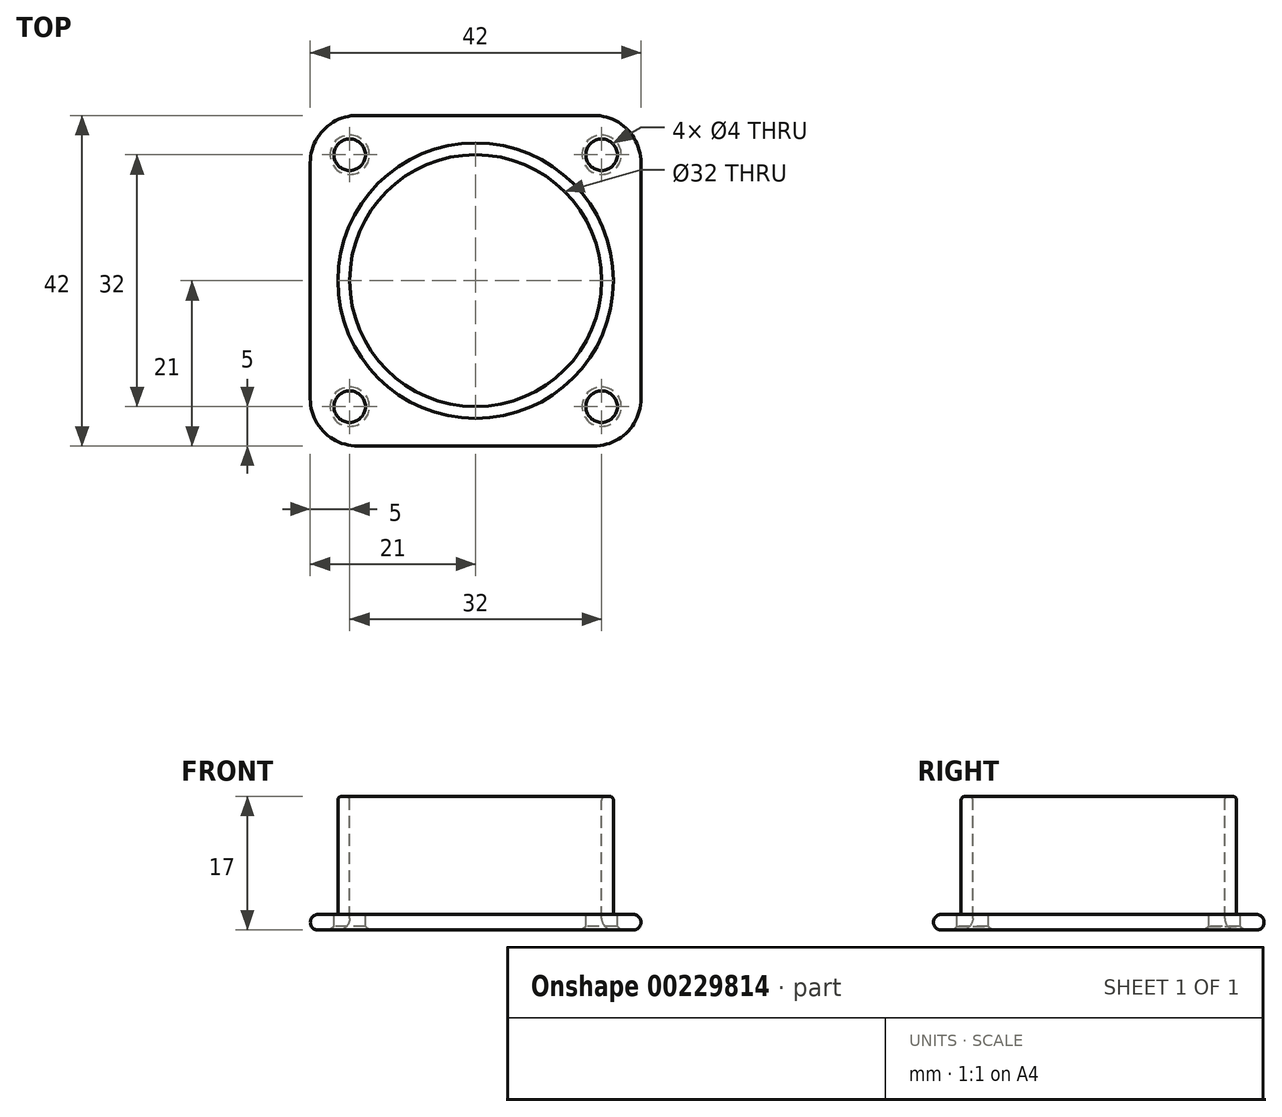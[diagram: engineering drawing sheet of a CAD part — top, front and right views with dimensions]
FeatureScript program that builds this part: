
annotation { "Feature Type Name" : "Feature", "Feature Type Description" : "" }
export const myFeature = defineFeature(function(context is Context, id is Id, definition is map)
    precondition{}
    {
        {
            var Q0;
            Q0=qCreatedBy(makeId("Top.planeOp"),FACE);
            var sketch = newSketch(context, id + "F0", { "sketchPlane" : qUnion([Q0])});
            skCircle(sketch, "E0", {"center": v(0, 0) * mm, "radius": 17.5 * mm});
            skLineSegment(sketch, "E1.bottom", {"start": v(21, 21) * mm, "end": v(-21, 21) * mm});
            skLineSegment(sketch, "E1.top", {"start": v(21, -21) * mm, "end": v(-21, -21) * mm});
            skLineSegment(sketch, "E1.left", {"start": v(21, 21) * mm, "end": v(21, -21) * mm});
            skLineSegment(sketch, "E1.right", {"start": v(-21, 21) * mm, "end": v(-21, -21) * mm});
            skLineSegment(sketch, "E2.bottom", {"start": v(-16, 16) * mm, "end": v(16, 16) * mm, "construction": true});
            skLineSegment(sketch, "E2.top", {"start": v(-16, -16) * mm, "end": v(16, -16) * mm, "construction": true});
            skLineSegment(sketch, "E2.left", {"start": v(-16, 16) * mm, "end": v(-16, -16) * mm, "construction": true});
            skLineSegment(sketch, "E2.right", {"start": v(16, 16) * mm, "end": v(16, -16) * mm, "construction": true});
            skCircle(sketch, "E3", {"center": v(0, 0) * mm, "radius": 16 * mm});
            skCircle(sketch, "E4", {"center": v(-16, 16) * mm, "radius": 2 * mm});
            skCircle(sketch, "E5", {"center": v(16, 16) * mm, "radius": 2 * mm});
            skCircle(sketch, "E6", {"center": v(16, -16) * mm, "radius": 2 * mm});
            skCircle(sketch, "E7", {"center": v(-16, -16) * mm, "radius": 2 * mm});
            skSolve(sketch);
        }
        {
            var Q0;
            Q0=makeQuery(id+"F0.imprint","IMPRINT",FACE,{"disambiguationData":[TD([[makeQuery(id+"F0.imprint","IMPRINT",EDGE,{"derivedFrom":sQuery(id+"F0.wireOp",EDGE,"E0")}),-1.0]])]});
            var Q1;
            Q1=makeQuery(id+"F0.imprint","IMPRINT",FACE,{"disambiguationData":[TD([[makeQuery(id+"F0.imprint","IMPRINT",EDGE,{"derivedFrom":sQuery(id+"F0.wireOp",EDGE,"E0")}),1.0]])]});
            extrude(context, id + "F1", {"entities" : qUnion([Q0, Q1]), "oppositeDirection" : true, "depth" : 2 * mm});
        }
        {
            var Q0;
            Q0=makeQuery(id+"F0.imprint","IMPRINT",FACE,{"disambiguationData":[TD([[makeQuery(id+"F0.imprint","IMPRINT",EDGE,{"derivedFrom":sQuery(id+"F0.wireOp",EDGE,"E0")}),1.0]])]});
            extrude(context, id + "F2", {"entities" : qUnion([Q0]), "operationType" : NewBodyOperationType.ADD, "depth" : 15 * mm});
        }
        {
            var Q0;
            Q0=makeQuery(id+"F1.opExtrude","SWEPT_EDGE",EDGE,{"disambiguationData":[OSD([sQuery(id+"F0.wireOp",EDGE,"E1.bottom"),sQuery(id+"F0.wireOp",EDGE,"E1.right")])]});
            var Q1;
            Q1=makeQuery(id+"F1.opExtrude","SWEPT_EDGE",EDGE,{"disambiguationData":[OSD([sQuery(id+"F0.wireOp",EDGE,"E1.top"),sQuery(id+"F0.wireOp",EDGE,"E1.right")])]});
            var Q2;
            Q2=makeQuery(id+"F1.opExtrude","SWEPT_EDGE",EDGE,{"disambiguationData":[OSD([sQuery(id+"F0.wireOp",EDGE,"E1.top"),sQuery(id+"F0.wireOp",EDGE,"E1.left")])]});
            var Q3;
            Q3=makeQuery(id+"F1.opExtrude","SWEPT_EDGE",EDGE,{"disambiguationData":[OSD([sQuery(id+"F0.wireOp",EDGE,"E1.bottom"),sQuery(id+"F0.wireOp",EDGE,"E1.left")])]});
            fillet(context, id + "F3", {"entities" : qUnion([Q0, Q1, Q2, Q3]), "radius" : 6 * mm, "tangentPropagation" : true, "allowEdgeOverflow" : false});
        }
        {
            var Q0;
            Q0=makeQuery(id+"F1.opExtrude","SWEPT_FACE",FACE,{"disambiguationData":[OSD([sQuery(id+"F0.wireOp",EDGE,"E1.left")])]});
            var Q1;
            Q1=makeQuery(id+"F3.opFillet","BLEND_FACE",FACE,{"disambiguationData":[OSD([sQuery(id+"F0.wireOp",EDGE,"E1.top"),sQuery(id+"F0.wireOp",EDGE,"E1.left")])]});
            var Q2;
            Q2=makeQuery(id+"F3.opFillet","BLEND_FACE",FACE,{"disambiguationData":[OSD([sQuery(id+"F0.wireOp",EDGE,"E1.bottom"),sQuery(id+"F0.wireOp",EDGE,"E1.left")])]});
            var Q3;
            Q3=makeQuery(id+"F1.opExtrude","SWEPT_FACE",FACE,{"disambiguationData":[OSD([sQuery(id+"F0.wireOp",EDGE,"E1.bottom")])]});
            var Q4;
            Q4=makeQuery(id+"F3.opFillet","BLEND_FACE",FACE,{"disambiguationData":[OSD([sQuery(id+"F0.wireOp",EDGE,"E1.bottom"),sQuery(id+"F0.wireOp",EDGE,"E1.right")])]});
            var Q5;
            Q5=makeQuery(id+"F1.opExtrude","SWEPT_FACE",FACE,{"disambiguationData":[OSD([sQuery(id+"F0.wireOp",EDGE,"E1.right")])]});
            var Q6;
            Q6=makeQuery(id+"F3.opFillet","BLEND_FACE",FACE,{"disambiguationData":[OSD([sQuery(id+"F0.wireOp",EDGE,"E1.top"),sQuery(id+"F0.wireOp",EDGE,"E1.right")])]});
            var Q7;
            Q7=makeQuery(id+"F1.opExtrude","SWEPT_FACE",FACE,{"disambiguationData":[OSD([sQuery(id+"F0.wireOp",EDGE,"E1.top")])]});
            fillet(context, id + "F4", {"entities" : qUnion([Q0, Q1, Q2, Q3, Q4, Q5, Q6, Q7]), "radius" : 1 * mm, "tangentPropagation" : true, "allowEdgeOverflow" : false});
        }
        {
            var Q0;
            Q0=makeQuery(id+"F1.opExtrude","CAP_EDGE",EDGE,{"disambiguationData":[OSD([sQuery(id+"F0.wireOp",EDGE,"E3")])],"isStart":false});
            var Q1;
            Q1=makeQuery(id+"F2.opExtrude","CAP_EDGE",EDGE,{"disambiguationData":[OSD([sQuery(id+"F0.wireOp",EDGE,"E0")])],"isStart":true});
            fillet(context, id + "F5", {"entities" : qUnion([Q0, Q1]), "radius" : 1.5 * mm, "tangentPropagation" : true, "allowEdgeOverflow" : false});
        }
        {
            var Q0;
            Q0=makeQuery(id+"F1.opExtrude","CAP_EDGE",EDGE,{"disambiguationData":[OSD([sQuery(id+"F0.wireOp",EDGE,"E7")])],"isStart":false});
            var Q1;
            Q1=makeQuery(id+"F1.opExtrude","CAP_EDGE",EDGE,{"disambiguationData":[OSD([sQuery(id+"F0.wireOp",EDGE,"E6")])],"isStart":false});
            var Q2;
            Q2=makeQuery(id+"F1.opExtrude","CAP_EDGE",EDGE,{"disambiguationData":[OSD([sQuery(id+"F0.wireOp",EDGE,"E5")])],"isStart":false});
            var Q3;
            Q3=makeQuery(id+"F1.opExtrude","CAP_EDGE",EDGE,{"disambiguationData":[OSD([sQuery(id+"F0.wireOp",EDGE,"E4")])],"isStart":false});
            chamfer(context, id + "F6", {"entities" : qUnion([Q0, Q1, Q2, Q3]), "width" : .5 * mm, "tangentPropagation" : true});
        }
        {
            var Q0;
            Q0=makeQuery(id+"F2.opExtrude","CAP_FACE",FACE,{"disambiguationData":[OSD([sQuery(id+"F0.wireOp",EDGE,"E0"),sQuery(id+"F0.wireOp",EDGE,"E3")])],"isStart":false});
            fillet(context, id + "F7", {"entities" : qUnion([Q0]), "radius" : .5 * mm, "tangentPropagation" : true, "allowEdgeOverflow" : false});
        }
    });
